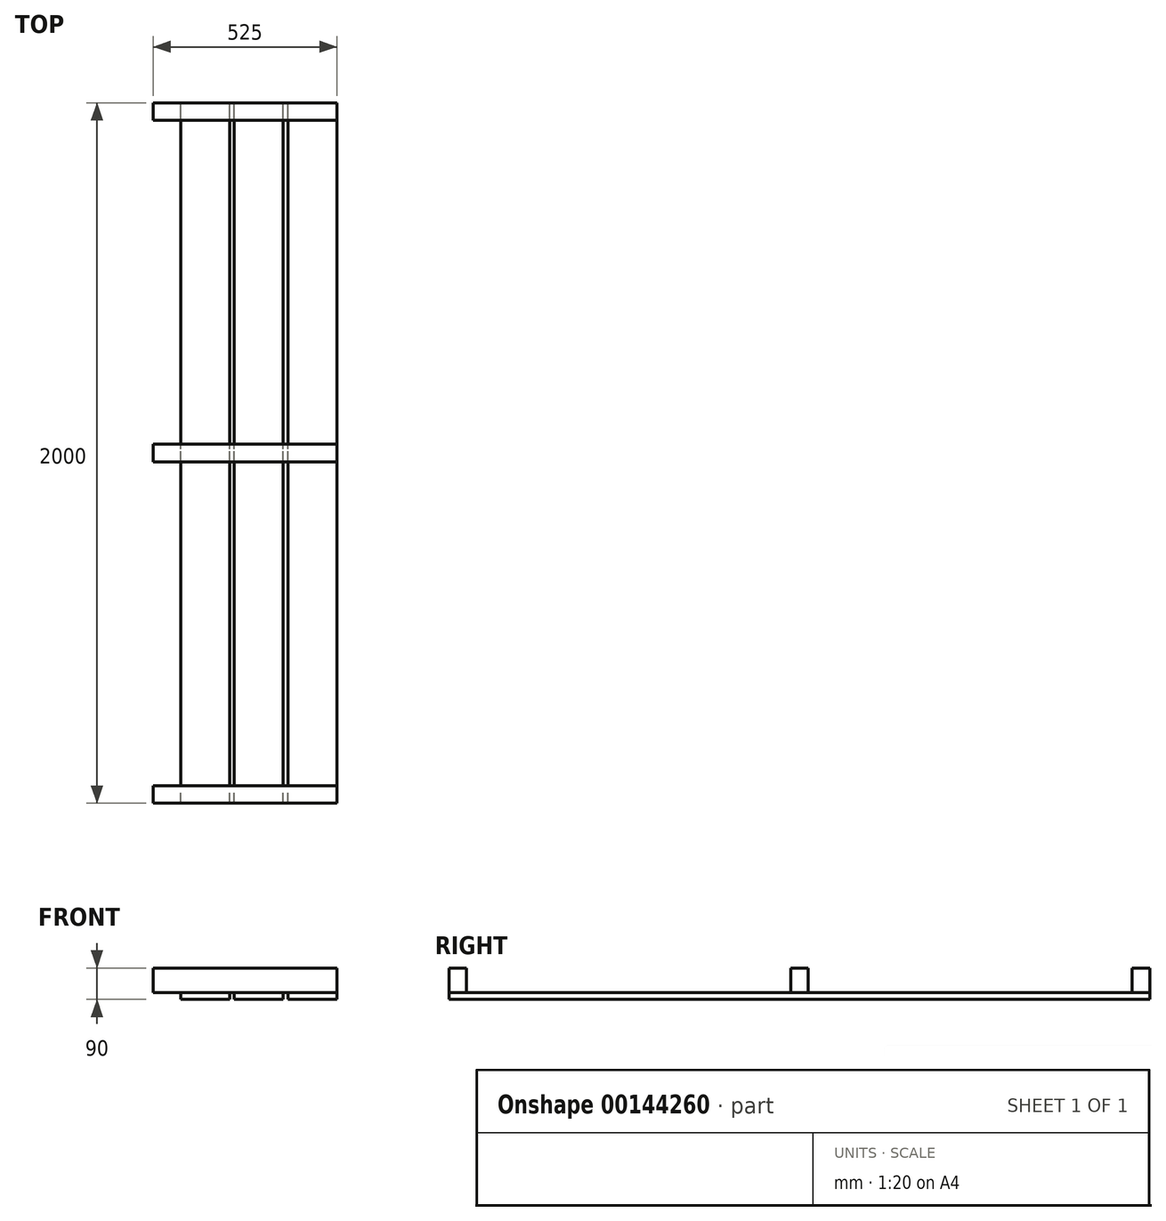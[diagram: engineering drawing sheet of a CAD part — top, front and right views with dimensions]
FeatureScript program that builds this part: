
annotation { "Feature Type Name" : "Feature", "Feature Type Description" : "" }
export const myFeature = defineFeature(function(context is Context, id is Id, definition is map)
    precondition{}
    {
        {
            var Q0;
            Q0=qCreatedBy(makeId("Front.planeOp"),FACE);
            var sketch = newSketch(context, id + "F0", { "sketchPlane" : qUnion([Q0])});
            skLineSegment(sketch, "E0.bottom", {"start": v(0, 0) * mm, "end": v(140, 0) * mm});
            skLineSegment(sketch, "E0.top", {"start": v(0, 20) * mm, "end": v(140, 20) * mm});
            skLineSegment(sketch, "E0.left", {"start": v(0, 0) * mm, "end": v(0, 20) * mm});
            skLineSegment(sketch, "E0.right", {"start": v(140, 0) * mm, "end": v(140, 20) * mm});
            skLineSegment(sketch, "E1.bottom", {"start": v(153, 0) * mm, "end": v(293, 0) * mm});
            skLineSegment(sketch, "E1.top", {"start": v(153, 20) * mm, "end": v(293, 20) * mm});
            skLineSegment(sketch, "E1.left", {"start": v(153, 0) * mm, "end": v(153, 20) * mm});
            skLineSegment(sketch, "E1.right", {"start": v(293, 0) * mm, "end": v(293, 20) * mm});
            skLineSegment(sketch, "E2.bottom", {"start": v(306, 0) * mm, "end": v(446, 0) * mm});
            skLineSegment(sketch, "E2.top", {"start": v(306, 20) * mm, "end": v(446, 20) * mm});
            skLineSegment(sketch, "E2.left", {"start": v(306, 0) * mm, "end": v(306, 20) * mm});
            skLineSegment(sketch, "E2.right", {"start": v(446, 0) * mm, "end": v(446, 20) * mm});
            skLineSegment(sketch, "E3.bottom", {"start": v(459, 0) * mm, "end": v(599, 0) * mm});
            skLineSegment(sketch, "E3.top", {"start": v(459, 20) * mm, "end": v(599, 20) * mm});
            skLineSegment(sketch, "E3.left", {"start": v(459, 0) * mm, "end": v(459, 20) * mm});
            skLineSegment(sketch, "E3.right", {"start": v(599, 0) * mm, "end": v(599, 20) * mm});
            skSolve(sketch);
        }
        {
            var Q0;
            Q0=makeQuery(id+"F0.imprint","IMPRINT",FACE,{"disambiguationData":[TD([[makeQuery(id+"F0.imprint","IMPRINT",EDGE,{"derivedFrom":sQuery(id+"F0.wireOp",EDGE,"E0.bottom")}),1.0]])]});
            var Q1;
            Q1=makeQuery(id+"F0.imprint","IMPRINT",FACE,{"disambiguationData":[TD([[makeQuery(id+"F0.imprint","IMPRINT",EDGE,{"derivedFrom":sQuery(id+"F0.wireOp",EDGE,"E1.bottom")}),1.0]])]});
            var Q2;
            Q2=makeQuery(id+"F0.imprint","IMPRINT",FACE,{"disambiguationData":[TD([[makeQuery(id+"F0.imprint","IMPRINT",EDGE,{"derivedFrom":sQuery(id+"F0.wireOp",EDGE,"E2.bottom")}),1.0]])]});
            extrude(context, id + "F1", {"entities" : qUnion([Q0, Q1, Q2]), "depth" : 2000 * mm});
        }
        {
            var Q0;
            Q0=makeQuery(id+"F1.opExtrude","SWEPT_FACE",FACE,{"disambiguationData":[OSD([sQuery(id+"F0.wireOp",EDGE,"E2.right")])]});
            var sketch = newSketch(context, id + "F2", { "sketchPlane" : qUnion([Q0])});
            skLineSegment(sketch, "E4.bottom", {"start": v(-2000, 20) * mm, "end": v(-1950, 20) * mm});
            skLineSegment(sketch, "E4.top", {"start": v(-2000, 90) * mm, "end": v(-1950, 90) * mm});
            skLineSegment(sketch, "E4.left", {"start": v(-2000, 20) * mm, "end": v(-2000, 90) * mm});
            skLineSegment(sketch, "E4.right", {"start": v(-1950, 20) * mm, "end": v(-1950, 90) * mm});
            skLineSegment(sketch, "E5.bottom", {"start": v(0, 20) * mm, "end": v(-50, 20) * mm});
            skLineSegment(sketch, "E5.top", {"start": v(0, 90) * mm, "end": v(-50, 90) * mm});
            skLineSegment(sketch, "E5.left", {"start": v(0, 20) * mm, "end": v(0, 90) * mm});
            skLineSegment(sketch, "E5.right", {"start": v(-50, 20) * mm, "end": v(-50, 90) * mm});
            skSolve(sketch);
        }
        {
            var Q0;
            Q0=makeQuery(id+"F2.imprint","IMPRINT",FACE,{"disambiguationData":[TD([[makeQuery(id+"F2.imprint","IMPRINT",EDGE,{"derivedFrom":sQuery(id+"F2.wireOp",EDGE,"E4.bottom")}),1.0]])]});
            var sketch = newSketch(context, id + "F3", { "sketchPlane" : qUnion([Q0])});
            skLineSegment(sketch, "E6.bottom", {"start": v(-1025, 20) * mm, "end": v(-975, 20) * mm});
            skLineSegment(sketch, "E6.top", {"start": v(-1025, 90) * mm, "end": v(-975, 90) * mm});
            skLineSegment(sketch, "E6.left", {"start": v(-1025, 20) * mm, "end": v(-1025, 90) * mm});
            skLineSegment(sketch, "E6.right", {"start": v(-975, 20) * mm, "end": v(-975, 90) * mm});
            skSolve(sketch);
        }
        {
            var Q0;
            Q0 = qSketchRegion(id + "F2", true);
            var Q1;
            Q1 = qSketchRegion(id + "F3", true);
            extrude(context, id + "F4", {"entities" : qUnion([Q0, Q1]), "oppositeDirection" : true, "depth" : 525 * mm});
        }
    });
